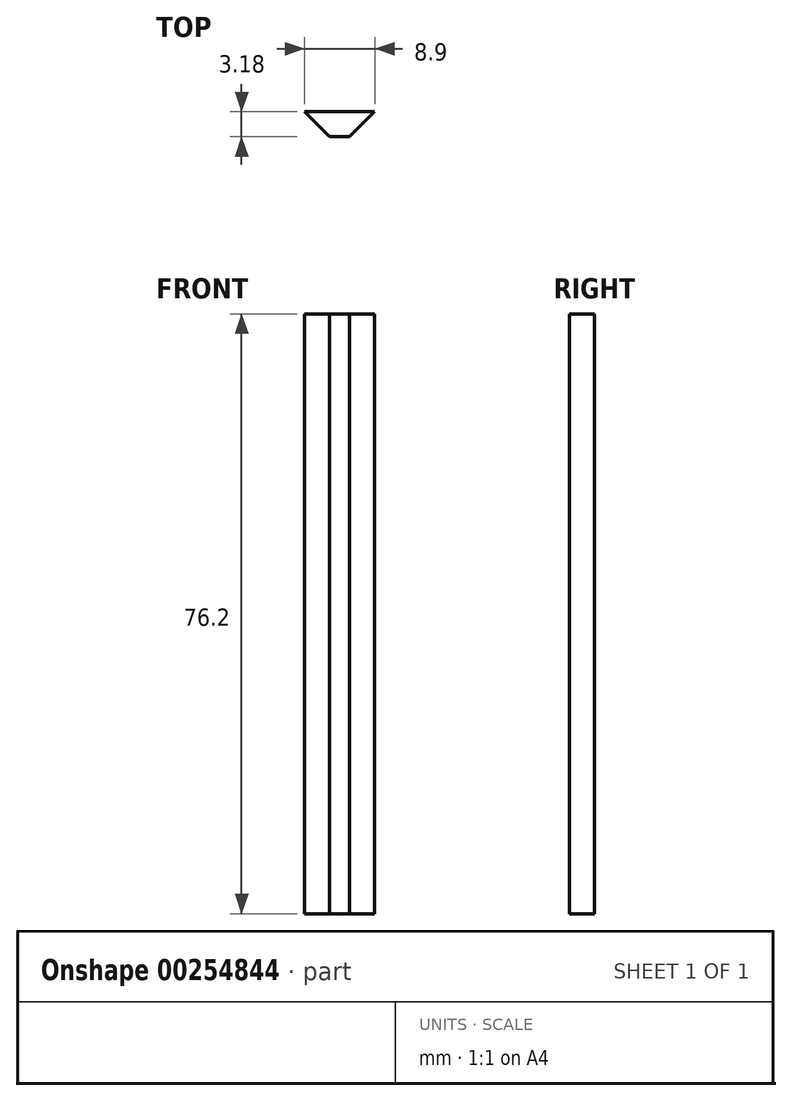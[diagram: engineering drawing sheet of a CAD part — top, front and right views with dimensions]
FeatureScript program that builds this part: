
annotation { "Feature Type Name" : "Feature", "Feature Type Description" : "" }
export const myFeature = defineFeature(function(context is Context, id is Id, definition is map)
    precondition{}
    {
        {
            var Q0;
            Q0=qCreatedBy(makeId("Front.planeOp"),FACE);
            var sketch = newSketch(context, id + "F0", { "sketchPlane" : qUnion([Q0])});
            skLineSegment(sketch, "E0.bottom", {"start": v(-6.35, -38.1) * mm, "end": v(6.35, -38.1) * mm});
            skLineSegment(sketch, "E0.top", {"start": v(-6.35, 38.1) * mm, "end": v(6.35, 38.1) * mm});
            skLineSegment(sketch, "E0.left", {"start": v(-6.35, -38.1) * mm, "end": v(-6.35, 38.1) * mm});
            skLineSegment(sketch, "E0.right", {"start": v(6.35, -38.1) * mm, "end": v(6.35, 38.1) * mm});
            skPoint(sketch, "E0.middle", {"position": v(0, 0) * mm});
            skSolve(sketch);
        }
        {
            var Q0;
            Q0=makeQuery(id+"F0.imprint","IMPRINT",FACE,{"disambiguationData":[TD([[makeQuery(id+"F0.imprint","IMPRINT",EDGE,{"derivedFrom":sQuery(id+"F0.wireOp",EDGE,"E0.bottom")}),1.0]])]});
            extrude(context, id + "F1", {"entities" : qUnion([Q0]), "endBound" : BoundingType.SYMMETRIC, "depth" : 3.17 * mm});
        }
        {
            var Q0;
            Q0=makeQuery(id+"F1.opExtrude","CAP_EDGE",EDGE,{"disambiguationData":[OSD([sQuery(id+"F0.wireOp",EDGE,"E0.left")])],"isStart":false});
            var Q1;
            Q1=makeQuery(id+"F1.opExtrude","CAP_EDGE",EDGE,{"disambiguationData":[OSD([sQuery(id+"F0.wireOp",EDGE,"E0.right")])],"isStart":false});
            chamfer(context, id + "F2", {"entities" : qUnion([Q0, Q1]), "width" : 5.08 * mm, "tangentPropagation" : true});
        }
    });
